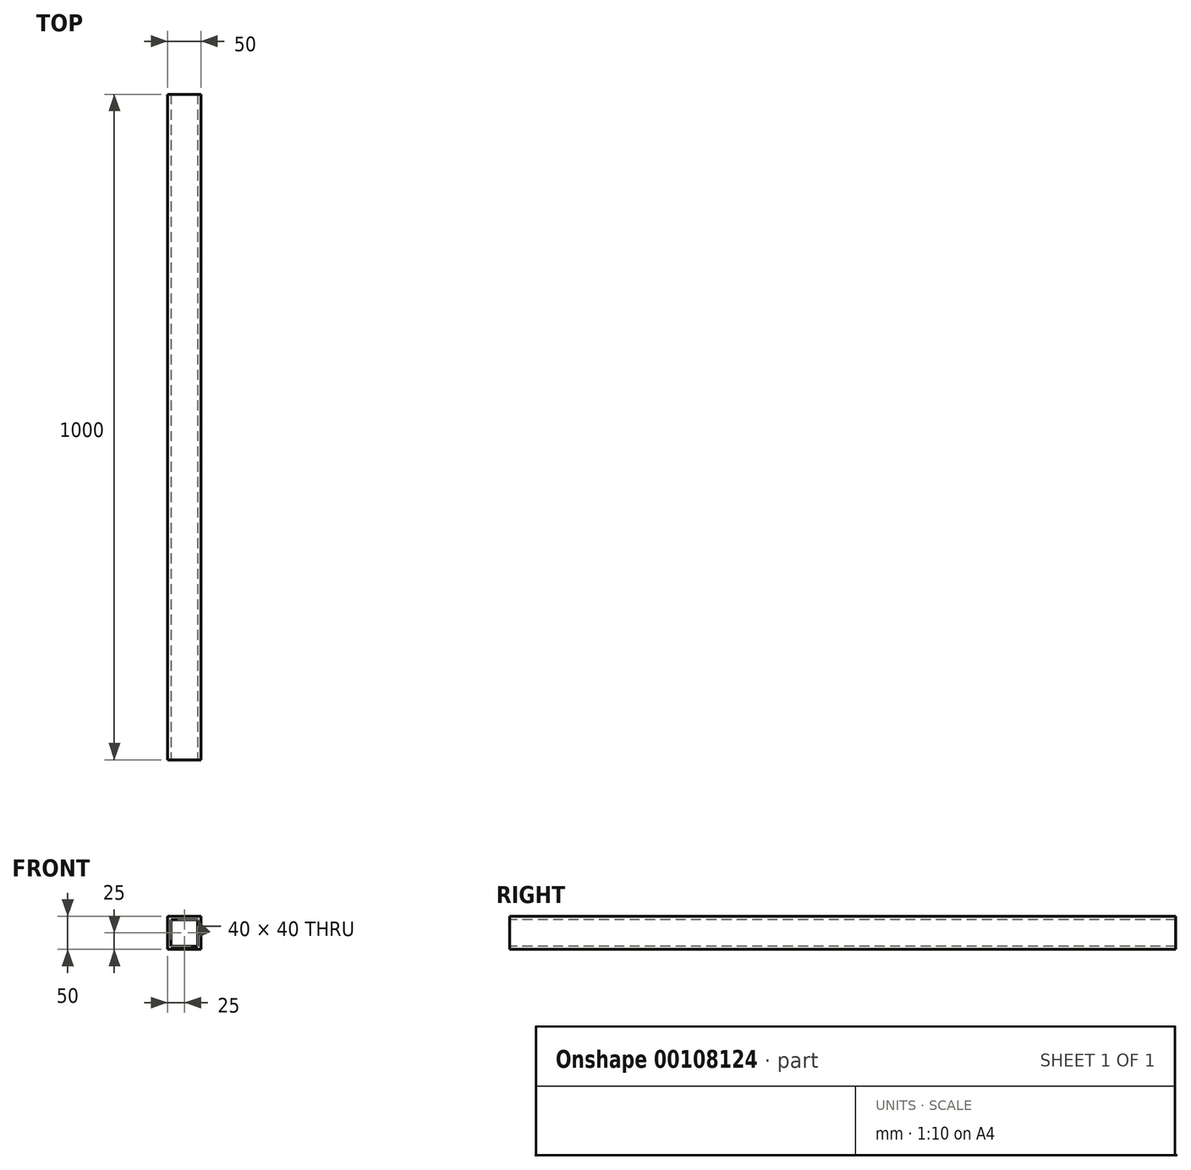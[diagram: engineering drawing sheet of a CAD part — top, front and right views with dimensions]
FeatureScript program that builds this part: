
annotation { "Feature Type Name" : "Feature", "Feature Type Description" : "" }
export const myFeature = defineFeature(function(context is Context, id is Id, definition is map)
    precondition{}
    {
        {
            var Q0;
            Q0=qCreatedBy(makeId("Front.planeOp"),FACE);
            var sketch = newSketch(context, id + "F0", { "sketchPlane" : qUnion([Q0])});
            skLineSegment(sketch, "E0.bottom", {"start": v(25, -25) * mm, "end": v(-25, -25) * mm});
            skLineSegment(sketch, "E0.top", {"start": v(25, 25) * mm, "end": v(-25, 25) * mm});
            skLineSegment(sketch, "E0.left", {"start": v(25, -25) * mm, "end": v(25, 25) * mm});
            skLineSegment(sketch, "E0.right", {"start": v(-25, -25) * mm, "end": v(-25, 25) * mm});
            skPoint(sketch, "E0.middle", {"position": v(0, 0) * mm});
            skLineSegment(sketch, "E1.bottom", {"start": v(20, -20) * mm, "end": v(-20, -20) * mm});
            skLineSegment(sketch, "E1.top", {"start": v(20, 20) * mm, "end": v(-20, 20) * mm});
            skLineSegment(sketch, "E1.left", {"start": v(20, -20) * mm, "end": v(20, 20) * mm});
            skLineSegment(sketch, "E1.right", {"start": v(-20, -20) * mm, "end": v(-20, 20) * mm});
            skSolve(sketch);
        }
        {
            var Q0;
            Q0=makeQuery(id+"F0.imprint","IMPRINT",FACE,{"disambiguationData":[TD([[makeQuery(id+"F0.imprint","IMPRINT",EDGE,{"derivedFrom":sQuery(id+"F0.wireOp",EDGE,"E0.bottom")}),-1.0]])]});
            extrude(context, id + "F1", {"entities" : qUnion([Q0]), "oppositeDirection" : true, "depth" : 1000 * mm});
        }
    });
